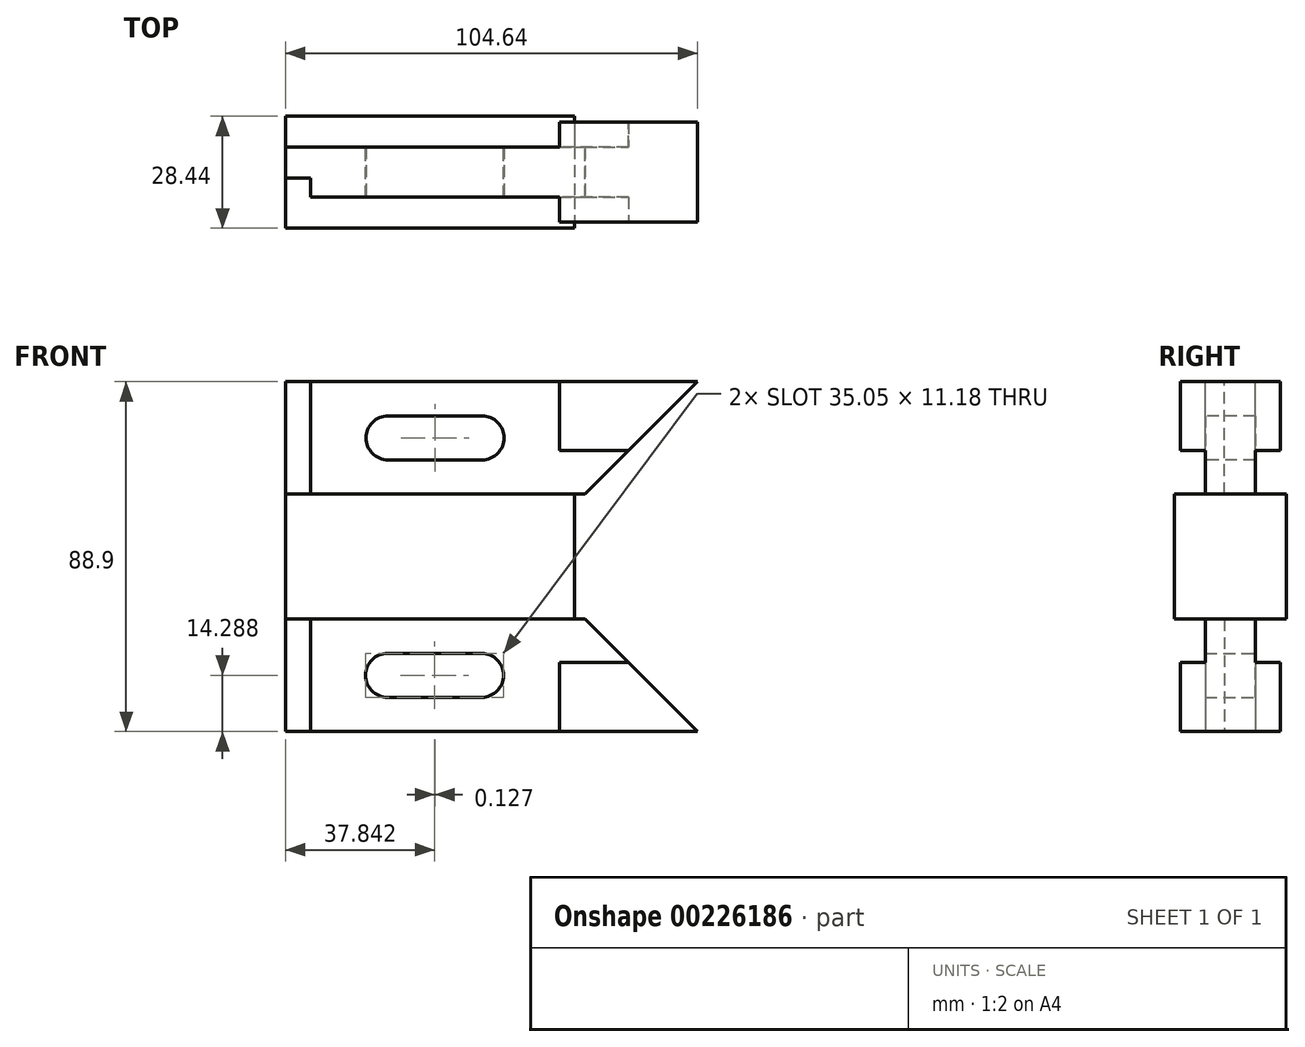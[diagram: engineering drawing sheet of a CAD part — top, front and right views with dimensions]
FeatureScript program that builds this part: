
annotation { "Feature Type Name" : "Feature", "Feature Type Description" : "" }
export const myFeature = defineFeature(function(context is Context, id is Id, definition is map)
    precondition{}
    {
        {
            var Q0;
            Q0=qCreatedBy(makeId("Front.planeOp"),FACE);
            var sketch = newSketch(context, id + "F0", { "sketchPlane" : qUnion([Q0])});
            skLineSegment(sketch, "E0.bottom", {"start": v(52.32, -44.45) * mm, "end": v(-52.32, -44.45) * mm});
            skLineSegment(sketch, "E0.top", {"start": v(52.32, 44.45) * mm, "end": v(-52.32, 44.45) * mm});
            skLineSegment(sketch, "E0.left", {"start": v(52.32, -44.45) * mm, "end": v(52.32, 44.45) * mm});
            skLineSegment(sketch, "E0.right", {"start": v(-52.32, -44.45) * mm, "end": v(-52.32, 44.45) * mm});
            skPoint(sketch, "E0.middle", {"position": v(0, 0) * mm});
            skLineSegment(sketch, "E1", {"start": v(-52.32, 15.87) * mm, "end": v(52.32, 15.87) * mm});
            skLineSegment(sketch, "E2", {"start": v(-52.32, -15.87) * mm, "end": v(52.32, -15.87) * mm});
            skSolve(sketch);
        }
        {
            var Q0;
            {var subQ0=sQuery(id+"F0.wireOp",EDGE,"E1");var subQ1=sQuery(id+"F0.wireOp",EDGE,"E0.left");var subQ2=makeQuery(id+"F0.imprint","INTERSECT",VERTEX,{"derivedFrom":[subQ1,subQ0]});Q0=makeQuery(id+"F0.imprint","IMPRINT",FACE,{"disambiguationData":[TD([[makeQuery(id+"F0.imprint","IMPRINT",EDGE,{"disambiguationData":[TD([[subQ2,1.0]])],"derivedFrom":subQ1}),1.0]])]});}
            extrude(context, id + "F1", {"entities" : qUnion([Q0]), "endBound" : BoundingType.SYMMETRIC, "depth" : 28.45 * mm});
        }
        {
            var Q0;
            {var subQ0=sQuery(id+"F0.wireOp",EDGE,"E0.top");Q0=makeQuery(id+"F0.imprint","IMPRINT",FACE,{"disambiguationData":[TD([[makeQuery(id+"F0.imprint","IMPRINT",EDGE,{"derivedFrom":subQ0}),1.0]])]});}
            var Q1;
            {var subQ0=sQuery(id+"F0.wireOp",EDGE,"E0.bottom");Q1=makeQuery(id+"F0.imprint","IMPRINT",FACE,{"disambiguationData":[TD([[makeQuery(id+"F0.imprint","IMPRINT",EDGE,{"derivedFrom":subQ0}),-1.0]])]});}
            extrude(context, id + "F2", {"entities" : qUnion([Q0, Q1]), "operationType" : NewBodyOperationType.ADD, "endBound" : BoundingType.SYMMETRIC, "depth" : 25.4 * mm});
        }
        {
            var Q0;
            Q0=makeQuery(id+"F2.opExtrude","SWEPT_FACE",FACE,{"disambiguationData":[OSD([sQuery(id+"F0.wireOp",EDGE,"E0.top")])]});
            var sketch = newSketch(context, id + "F3", { "sketchPlane" : qUnion([Q0])});
            skLineSegment(sketch, "E3", {"start": v(-52.32, 6.35) * mm, "end": v(17.27, 6.35) * mm});
            skLineSegment(sketch, "E4", {"start": v(-52.32, -1.52) * mm, "end": v(-45.97, -1.52) * mm});
            skLineSegment(sketch, "E5", {"start": v(-45.97, -1.52) * mm, "end": v(-45.97, -6.35) * mm});
            skLineSegment(sketch, "E6", {"start": v(-45.97, -6.35) * mm, "end": v(17.27, -6.35) * mm});
            skLineSegment(sketch, "E7.0", {"start": v(52.32, 12.7) * mm, "end": v(-52.32, 12.7) * mm});
            skLineSegment(sketch, "E8.0", {"start": v(52.32, -12.7) * mm, "end": v(-52.32, -12.7) * mm});
            skLineSegment(sketch, "E9", {"start": v(17.27, 6.35) * mm, "end": v(17.27, 12.7) * mm});
            skLineSegment(sketch, "E10", {"start": v(17.27, -6.35) * mm, "end": v(17.27, -12.7) * mm});
            skLineSegment(sketch, "E11", {"start": v(17.27, 12.7) * mm, "end": v(17.27, 6.35) * mm});
            skLineSegment(sketch, "E12", {"start": v(-52.32, 6.35) * mm, "end": v(-52.32, -1.52) * mm});
            skSolve(sketch);
        }
        {
            var Q0;
            Q0=makeQuery(id+"F2.opExtrude","SWEPT_FACE",FACE,{"disambiguationData":[OSD([sQuery(id+"F0.wireOp",EDGE,"E0.bottom")])]});
            var sketch = newSketch(context, id + "F4", { "sketchPlane" : qUnion([Q0])});
            skLineSegment(sketch, "E13", {"start": v(17.27, 12.7) * mm, "end": v(17.27, 6.35) * mm});
            skLineSegment(sketch, "E14", {"start": v(17.27, 6.35) * mm, "end": v(-45.97, 6.35) * mm});
            skLineSegment(sketch, "E15", {"start": v(-45.97, 6.35) * mm, "end": v(-45.97, 1.52) * mm});
            skLineSegment(sketch, "E16", {"start": v(-45.97, 1.52) * mm, "end": v(-52.32, 1.52) * mm});
            skLineSegment(sketch, "E17", {"start": v(-52.32, -6.34) * mm, "end": v(17.27, -6.34) * mm});
            skLineSegment(sketch, "E18", {"start": v(17.27, -6.34) * mm, "end": v(17.27, -12.7) * mm});
            skLineSegment(sketch, "E19.0", {"start": v(52.32, -12.7) * mm, "end": v(-52.32, -12.7) * mm});
            skLineSegment(sketch, "E20.0.1", {"start": v(-52.32, -12.7) * mm, "end": v(-52.32, -14.22) * mm});
            skLineSegment(sketch, "E20.0.2", {"start": v(-52.32, -14.22) * mm, "end": v(52.32, -14.22) * mm});
            skLineSegment(sketch, "E20.0.3", {"start": v(52.32, -14.22) * mm, "end": v(52.32, -12.7) * mm});
            skLineSegment(sketch, "E21.2", {"start": v(-52.32, -12.7) * mm, "end": v(52.32, -12.7) * mm});
            skLineSegment(sketch, "E21.3", {"start": v(-52.32, -12.7) * mm, "end": v(52.32, -12.7) * mm});
            skSolve(sketch);
        }
        {
            var Q0;
            {var subQ5=sQuery(id+"F4.wireOp",EDGE,"E13");Q0=makeQuery(id+"F4.imprint","IMPRINT",FACE,{"disambiguationData":[TD([[makeQuery(id+"F4.imprint","IMPRINT",EDGE,{"derivedFrom":subQ5}),-1.0]])]});}
            var Q1;
            {var subQ0=sQuery(id+"F4.wireOp",EDGE,"E17");Q1=makeQuery(id+"F4.imprint","IMPRINT",FACE,{"disambiguationData":[TD([[makeQuery(id+"F4.imprint","IMPRINT",EDGE,{"derivedFrom":subQ0}),-1.0]])]});}
            extrude(context, id + "F5", {"entities" : qUnion([Q0, Q1]), "operationType" : NewBodyOperationType.REMOVE, "oppositeDirection" : true, "depth" : 28.57 * mm});
        }
        {
            var Q0;
            {var subQ0=sQuery(id+"F3.wireOp",EDGE,"E3");Q0=makeQuery(id+"F3.imprint","IMPRINT",FACE,{"disambiguationData":[TD([[makeQuery(id+"F3.imprint","IMPRINT",EDGE,{"derivedFrom":subQ0}),1.0]])]});}
            var Q1;
            {var subQ4=sQuery(id+"F3.wireOp",EDGE,"E4");Q1=makeQuery(id+"F3.imprint","IMPRINT",FACE,{"disambiguationData":[TD([[makeQuery(id+"F3.imprint","IMPRINT",EDGE,{"derivedFrom":subQ4}),-1.0]])]});}
            extrude(context, id + "F6", {"entities" : qUnion([Q0, Q1]), "operationType" : NewBodyOperationType.REMOVE, "oppositeDirection" : true, "depth" : 28.57 * mm});
        }
        {
            var Q0;
            Q0=qCreatedBy(makeId("Right.planeOp"),FACE);
            var sketch = newSketch(context, id + "F7", { "sketchPlane" : qUnion([Q0])});
            skLineSegment(sketch, "E22", {"start": v(-6.35, 26.92) * mm, "end": v(-12.7, 26.92) * mm});
            skLineSegment(sketch, "E23", {"start": v(6.35, 26.92) * mm, "end": v(12.7, 26.92) * mm});
            skLineSegment(sketch, "E24", {"start": v(6.34, -26.92) * mm, "end": v(12.7, -26.92) * mm});
            skLineSegment(sketch, "E25", {"start": v(-6.35, -26.92) * mm, "end": v(-12.7, -26.92) * mm});
            skLineSegment(sketch, "E26.0", {"start": v(-12.7, 15.88) * mm, "end": v(-12.7, 44.45) * mm});
            skLineSegment(sketch, "E27.0", {"start": v(-6.35, 15.87) * mm, "end": v(-6.35, 44.45) * mm});
            skLineSegment(sketch, "E28.0", {"start": v(6.35, 15.87) * mm, "end": v(6.35, 44.45) * mm});
            skLineSegment(sketch, "E29.0", {"start": v(12.7, -15.87) * mm, "end": v(12.7, -44.45) * mm});
            skLineSegment(sketch, "E30.0", {"start": v(6.34, -15.88) * mm, "end": v(6.34, -44.45) * mm});
            skLineSegment(sketch, "E31.0", {"start": v(-6.35, -15.88) * mm, "end": v(-6.35, -44.45) * mm});
            skLineSegment(sketch, "E32.0", {"start": v(-12.7, -15.88) * mm, "end": v(-12.7, -44.45) * mm});
            skLineSegment(sketch, "E33.0", {"start": v(12.7, 15.88) * mm, "end": v(12.7, 44.45) * mm});
            skLineSegment(sketch, "E34", {"start": v(12.7, 15.88) * mm, "end": v(6.35, 15.87) * mm});
            skLineSegment(sketch, "E35", {"start": v(12.7, 44.45) * mm, "end": v(6.35, 44.45) * mm});
            skLineSegment(sketch, "E36", {"start": v(-6.35, 44.45) * mm, "end": v(-12.7, 44.45) * mm});
            skLineSegment(sketch, "E37", {"start": v(-6.35, 15.87) * mm, "end": v(-12.7, 15.88) * mm});
            skLineSegment(sketch, "E38", {"start": v(-6.35, -15.88) * mm, "end": v(-12.7, -15.88) * mm});
            skLineSegment(sketch, "E39", {"start": v(-6.35, -44.45) * mm, "end": v(-12.7, -44.45) * mm});
            skLineSegment(sketch, "E40", {"start": v(12.7, -44.45) * mm, "end": v(6.34, -44.45) * mm});
            skLineSegment(sketch, "E41", {"start": v(12.7, -15.87) * mm, "end": v(6.34, -15.88) * mm});
            skSolve(sketch);
        }
        {
            var Q0;
            {var subQ0=sQuery(id+"F7.wireOp",EDGE,"E22");Q0=makeQuery(id+"F7.imprint","IMPRINT",FACE,{"disambiguationData":[TD([[makeQuery(id+"F7.imprint","IMPRINT",EDGE,{"derivedFrom":subQ0}),1.0]])]});}
            var Q1;
            {var subQ0=sQuery(id+"F7.wireOp",EDGE,"E23");Q1=makeQuery(id+"F7.imprint","IMPRINT",FACE,{"disambiguationData":[TD([[makeQuery(id+"F7.imprint","IMPRINT",EDGE,{"derivedFrom":subQ0}),-1.0]])]});}
            var Q2;
            {var subQ0=sQuery(id+"F7.wireOp",EDGE,"E24");Q2=makeQuery(id+"F7.imprint","IMPRINT",FACE,{"disambiguationData":[TD([[makeQuery(id+"F7.imprint","IMPRINT",EDGE,{"derivedFrom":subQ0}),1.0]])]});}
            var Q3;
            {var subQ0=sQuery(id+"F7.wireOp",EDGE,"E25");Q3=makeQuery(id+"F7.imprint","IMPRINT",FACE,{"disambiguationData":[TD([[makeQuery(id+"F7.imprint","IMPRINT",EDGE,{"derivedFrom":subQ0}),-1.0]])]});}
            extrude(context, id + "F8", {"entities" : qUnion([Q0, Q1, Q2, Q3]), "operationType" : NewBodyOperationType.REMOVE, "endBound" : BoundingType.THROUGH_ALL, "depth" : 25.4 * mm});
        }
        {
            var Q0;
            Q0=makeQuery(id+"F1.opExtrude","CAP_FACE",FACE,{"disambiguationData":[OSD([sQuery(id+"F0.wireOp",EDGE,"E0.left"),sQuery(id+"F0.wireOp",EDGE,"E0.right"),sQuery(id+"F0.wireOp",EDGE,"E1"),sQuery(id+"F0.wireOp",EDGE,"E2")])],"isStart":false});
            var sketch = newSketch(context, id + "F9", { "sketchPlane" : qUnion([Q0])});
            skLineSegment(sketch, "E42", {"start": v(21.08, 15.87) * mm, "end": v(21.08, -15.87) * mm});
            skLineSegment(sketch, "E43.0", {"start": v(-52.32, 15.87) * mm, "end": v(52.32, 15.87) * mm});
            skLineSegment(sketch, "E44.0", {"start": v(-52.32, -15.87) * mm, "end": v(52.32, -15.87) * mm});
            skLineSegment(sketch, "E45.0", {"start": v(52.32, -44.45) * mm, "end": v(52.32, 44.45) * mm});
            skSolve(sketch);
        }
        {
            var Q0;
            {var subQ0=sQuery(id+"F9.wireOp",EDGE,"E42");Q0=makeQuery(id+"F9.imprint","IMPRINT",FACE,{"disambiguationData":[TD([[makeQuery(id+"F9.imprint","IMPRINT",EDGE,{"derivedFrom":subQ0}),1.0]])]});}
            extrude(context, id + "F10", {"entities" : qUnion([Q0]), "operationType" : NewBodyOperationType.REMOVE, "endBound" : BoundingType.THROUGH_ALL, "oppositeDirection" : true, "depth" : 25.4 * mm});
        }
        {
            var Q0;
            Q0=makeQuery(id+"F8.boolean.opBoolean","MERGE",FACE,{"derivedFrom":[makeQuery(id+"F5.boolean.opBoolean","COPY",FACE,{"derivedFrom":makeQuery(id+"F5.opExtrude","SWEPT_FACE",FACE,{"disambiguationData":[OSD([sQuery(id+"F4.wireOp",EDGE,"E14")])]})}),makeQuery(id+"F8.opExtrude","SWEPT_FACE",FACE,{"disambiguationData":[OSD([sQuery(id+"F7.wireOp",EDGE,"E31.0")])]})]});
            var sketch = newSketch(context, id + "F11", { "sketchPlane" : qUnion([Q0])});
            skLineSegment(sketch, "E46", {"start": v(52.32, -44.45) * mm, "end": v(23.75, -15.88) * mm});
            skLineSegment(sketch, "E47.0", {"start": v(-52.32, -15.87) * mm, "end": v(52.32, -15.87) * mm});
            skLineSegment(sketch, "E48.0", {"start": v(52.32, -44.45) * mm, "end": v(52.32, 44.45) * mm});
            skSolve(sketch);
        }
        {
            var Q0;
            {var subQ0=sQuery(id+"F11.wireOp",EDGE,"E47.0");var subQ5=sQuery(id+"F11.wireOp",EDGE,"E48.0");var subQ6=makeQuery(id+"F11.imprint","INTERSECT",VERTEX,{"derivedFrom":[subQ0,subQ5]});Q0=makeQuery(id+"F11.imprint","IMPRINT",FACE,{"disambiguationData":[TD([[makeQuery(id+"F11.imprint","IMPRINT",EDGE,{"disambiguationData":[TD([[subQ6,-1.0]])],"derivedFrom":subQ0}),1.0]])]});}
            extrude(context, id + "F12", {"entities" : qUnion([Q0]), "operationType" : NewBodyOperationType.REMOVE, "endBound" : BoundingType.THROUGH_ALL, "oppositeDirection" : true, "depth" : 25.4 * mm});
        }
        {
            var Q0;
            Q0=makeQuery(id+"F2.opExtrude","CAP_FACE",FACE,{"disambiguationData":[OSD([sQuery(id+"F0.wireOp",EDGE,"E0.bottom"),sQuery(id+"F0.wireOp",EDGE,"E0.left"),sQuery(id+"F0.wireOp",EDGE,"E0.right"),sQuery(id+"F0.wireOp",EDGE,"E2")])],"isStart":false});
            var sketch = newSketch(context, id + "F13", { "sketchPlane" : qUnion([Q0])});
            skLineSegment(sketch, "E49", {"start": v(52.32, -44.45) * mm, "end": v(34.8, -26.92) * mm});
            skSolve(sketch);
        }
        {
            var Q0;
            {var subQ0=sQuery(id+"F13.wireOp",EDGE,"E49");Q0=makeQuery(id+"F13.imprint","IMPRINT",FACE,{"disambiguationData":[TD([[makeQuery(id+"F13.imprint","IMPRINT",EDGE,{"derivedFrom":subQ0}),-1.0]])]});}
            extrude(context, id + "F14", {"entities" : qUnion([Q0]), "operationType" : NewBodyOperationType.REMOVE, "endBound" : BoundingType.THROUGH_ALL, "oppositeDirection" : true, "depth" : 25.4 * mm});
        }
        {
            var Q0;
            Q0=makeQuery(id+"F2.opExtrude","CAP_FACE",FACE,{"disambiguationData":[OSD([sQuery(id+"F0.wireOp",EDGE,"E0.top"),sQuery(id+"F0.wireOp",EDGE,"E0.left"),sQuery(id+"F0.wireOp",EDGE,"E0.right"),sQuery(id+"F0.wireOp",EDGE,"E1")])],"isStart":true});
            var sketch = newSketch(context, id + "F15", { "sketchPlane" : qUnion([Q0])});
            skLineSegment(sketch, "E50", {"start": v(-52.32, 44.45) * mm, "end": v(-34.8, 26.92) * mm});
            skSolve(sketch);
        }
        {
            var Q0;
            {var subQ0=sQuery(id+"F15.wireOp",EDGE,"E50");Q0=makeQuery(id+"F15.imprint","IMPRINT",FACE,{"disambiguationData":[TD([[makeQuery(id+"F15.imprint","IMPRINT",EDGE,{"derivedFrom":subQ0}),-1.0]])]});}
            extrude(context, id + "F16", {"entities" : qUnion([Q0]), "operationType" : NewBodyOperationType.REMOVE, "endBound" : BoundingType.THROUGH_ALL, "oppositeDirection" : true, "depth" : 25.4 * mm});
        }
        {
            var Q0;
            Q0=makeQuery(id+"F8.boolean.opBoolean","MERGE",FACE,{"derivedFrom":[makeQuery(id+"F6.boolean.opBoolean","COPY",FACE,{"derivedFrom":makeQuery(id+"F6.opExtrude","SWEPT_FACE",FACE,{"disambiguationData":[OSD([sQuery(id+"F3.wireOp",EDGE,"E3")])]})}),makeQuery(id+"F8.opExtrude","SWEPT_FACE",FACE,{"disambiguationData":[OSD([sQuery(id+"F7.wireOp",EDGE,"E28.0")])]})]});
            var sketch = newSketch(context, id + "F17", { "sketchPlane" : qUnion([Q0])});
            skLineSegment(sketch, "E51", {"start": v(-34.8, 26.92) * mm, "end": v(-23.75, 15.87) * mm});
            skSolve(sketch);
        }
        {
            var Q0;
            {var subQ0=sQuery(id+"F17.wireOp",EDGE,"E51");Q0=makeQuery(id+"F17.imprint","IMPRINT",FACE,{"disambiguationData":[TD([[makeQuery(id+"F17.imprint","IMPRINT",EDGE,{"derivedFrom":subQ0}),-1.0]])]});}
            extrude(context, id + "F18", {"entities" : qUnion([Q0]), "operationType" : NewBodyOperationType.REMOVE, "endBound" : BoundingType.THROUGH_ALL, "oppositeDirection" : true, "depth" : 25.4 * mm});
        }
        {
            var Q0;
            Q0=makeQuery(id+"F8.boolean.opBoolean","MERGE",FACE,{"derivedFrom":[makeQuery(id+"F5.boolean.opBoolean","COPY",FACE,{"derivedFrom":makeQuery(id+"F5.opExtrude","SWEPT_FACE",FACE,{"disambiguationData":[OSD([sQuery(id+"F4.wireOp",EDGE,"E17")])]})}),makeQuery(id+"F8.opExtrude","SWEPT_FACE",FACE,{"disambiguationData":[OSD([sQuery(id+"F7.wireOp",EDGE,"E30.0")])]})]});
            var sketch = newSketch(context, id + "F19", { "sketchPlane" : qUnion([Q0])});
            skLineSegment(sketch, "E52", {"start": v(52.32, -30.16) * mm, "end": v(-17.27, -30.16) * mm, "construction": true});
            skCircle(sketch, "E53", {"center": v(26.42, -30.16) * mm, "radius": 5.59 * mm});
            skCircle(sketch, "E54", {"center": v(2.54, -30.16) * mm, "radius": 5.59 * mm});
            skLineSegment(sketch, "E55", {"start": v(26.42, -24.57) * mm, "end": v(2.54, -24.57) * mm});
            skLineSegment(sketch, "E56", {"start": v(2.54, -35.75) * mm, "end": v(26.42, -35.75) * mm});
            skSolve(sketch);
        }
        {
            var Q0;
            Q0=makeQuery(id+"F8.boolean.opBoolean","MERGE",FACE,{"derivedFrom":[makeQuery(id+"F6.boolean.opBoolean","COPY",FACE,{"derivedFrom":makeQuery(id+"F6.opExtrude","SWEPT_FACE",FACE,{"disambiguationData":[OSD([sQuery(id+"F3.wireOp",EDGE,"E6")])]})}),makeQuery(id+"F8.opExtrude","SWEPT_FACE",FACE,{"disambiguationData":[OSD([sQuery(id+"F7.wireOp",EDGE,"E27.0")])]})]});
            var sketch = newSketch(context, id + "F20", { "sketchPlane" : qUnion([Q0])});
            skLineSegment(sketch, "E57", {"start": v(-45.97, 30.16) * mm, "end": v(17.27, 30.16) * mm, "construction": true});
            skCircle(sketch, "E58", {"center": v(-26.29, 30.16) * mm, "radius": 5.59 * mm});
            skCircle(sketch, "E59", {"center": v(-2.41, 30.16) * mm, "radius": 5.59 * mm});
            skLineSegment(sketch, "E60", {"start": v(-26.29, 35.75) * mm, "end": v(-2.41, 35.75) * mm});
            skLineSegment(sketch, "E61", {"start": v(-26.29, 24.57) * mm, "end": v(-2.41, 24.57) * mm});
            skSolve(sketch);
        }
        {
            var Q0;
            Q0 = qSketchRegion(id + "F20", true);
            extrude(context, id + "F21", {"entities" : qUnion([Q0]), "operationType" : NewBodyOperationType.REMOVE, "endBound" : BoundingType.THROUGH_ALL, "oppositeDirection" : true, "depth" : 25.4 * mm});
        }
        {
            var Q0;
            {var subQ0=sQuery(id+"F19.wireOp",EDGE,"E53");var subQ1=makeQuery(id+"F19.imprint","INTERSECT",VERTEX,{"derivedFrom":[subQ0,sQuery(id+"F19.wireOp",EDGE,"E55")]});Q0=makeQuery(id+"F19.imprint","IMPRINT",FACE,{"disambiguationData":[TD([[makeQuery(id+"F19.imprint","IMPRINT",EDGE,{"disambiguationData":[TD([[subQ1,-1.0]])],"derivedFrom":subQ0}),1.0]])]});}
            var Q1;
            {var subQ0=sQuery(id+"F19.wireOp",EDGE,"E55");Q1=makeQuery(id+"F19.imprint","IMPRINT",FACE,{"disambiguationData":[TD([[makeQuery(id+"F19.imprint","IMPRINT",EDGE,{"derivedFrom":subQ0}),1.0]])]});}
            var Q2;
            {var subQ0=sQuery(id+"F19.wireOp",EDGE,"E54");var subQ1=makeQuery(id+"F19.imprint","INTERSECT",VERTEX,{"derivedFrom":[subQ0,sQuery(id+"F19.wireOp",EDGE,"E55")]});Q2=makeQuery(id+"F19.imprint","IMPRINT",FACE,{"disambiguationData":[TD([[makeQuery(id+"F19.imprint","IMPRINT",EDGE,{"disambiguationData":[TD([[subQ1,-1.0]])],"derivedFrom":subQ0}),1.0]])]});}
            extrude(context, id + "F22", {"entities" : qUnion([Q0, Q1, Q2]), "operationType" : NewBodyOperationType.REMOVE, "endBound" : BoundingType.THROUGH_ALL, "oppositeDirection" : true, "depth" : 25.4 * mm});
        }
    });
